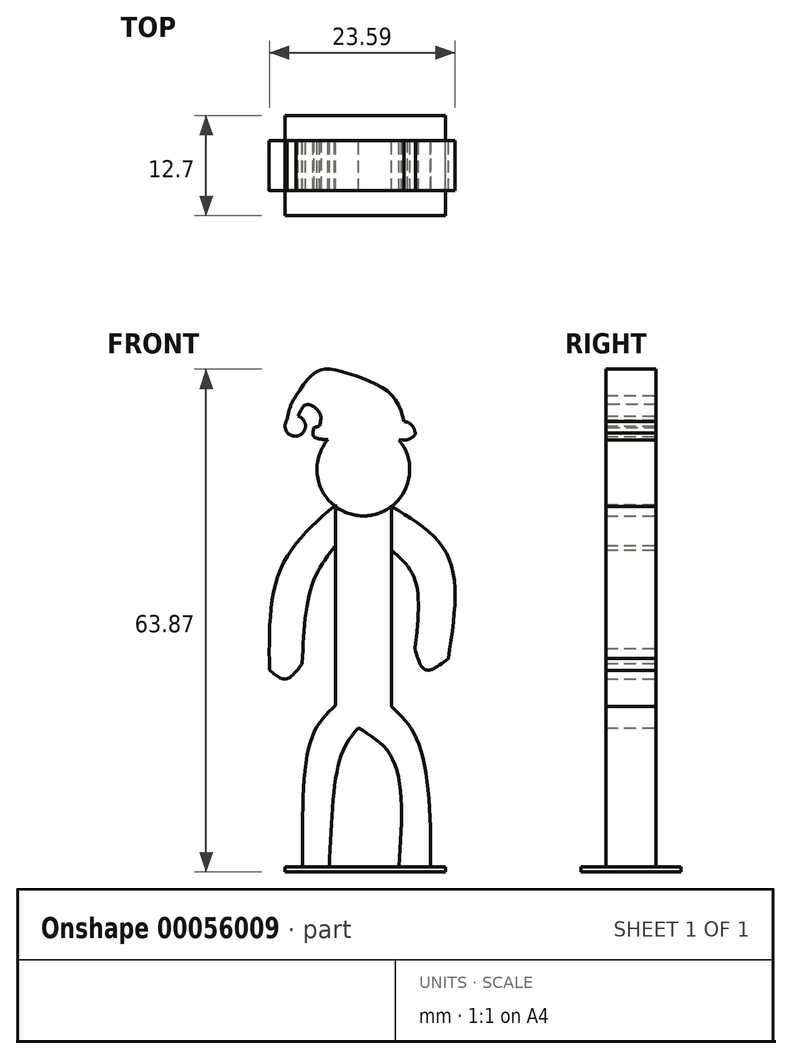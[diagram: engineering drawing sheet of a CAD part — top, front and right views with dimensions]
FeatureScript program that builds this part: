
annotation { "Feature Type Name" : "Feature", "Feature Type Description" : "" }
export const myFeature = defineFeature(function(context is Context, id is Id, definition is map)
    precondition{}
    {
        {
            var Q0;
            Q0=qCreatedBy(makeId("Front.planeOp"),FACE);
            var sketch = newSketch(context, id + "F0", { "sketchPlane" : qUnion([Q0])});
            skFitSpline(sketch, "E0", {"points": [v(8.78, 51.91) * mm, v(1.84, 43.84) * mm, v(0.38, 30.92) * mm], "startDerivative": vector(-17.42, -15.2) * mm, "endDerivative": vector(0.33, -26.61) * mm});
            skFitSpline(sketch, "E1", {"points": [v(15.91, 51.68) * mm, v(23.1, 45.3) * mm, v(23.1, 32.37) * mm], "startDerivative": vector(19.1, -11.4) * mm, "endDerivative": vector(-4.16, -26.82) * mm});
            skFitSpline(sketch, "E2", {"points": [v(15.91, 46.14) * mm, v(18.86, 42.38) * mm, v(18.86, 33.63) * mm], "startDerivative": vector(8.41, -7.48) * mm, "endDerivative": vector(-2, -17.05) * mm});
            skFitSpline(sketch, "E3", {"points": [v(8.78, 46.73) * mm, v(5.8, 41.75) * mm, v(4.55, 31.75) * mm], "startDerivative": vector(-7.92, -10.28) * mm, "endDerivative": vector(-0.86, -19.32) * mm});
            skFitSpline(sketch, "E4", {"points": [v(0.38, 30.92) * mm, v(2.47, 29.78) * mm, v(4.55, 31.75) * mm], "startDerivative": vector(4.49, -3.84) * mm, "endDerivative": vector(3.86, 5.36) * mm});
            skFitSpline(sketch, "E5", {"points": [v(18.86, 33.63) * mm, v(20.26, 30.92) * mm, v(23.1, 32.37) * mm], "startDerivative": vector(2.14, -7.53) * mm, "endDerivative": vector(6.3, 4.98) * mm});
            skLineSegment(sketch, "E6", {"start": v(8.78, 51.91) * mm, "end": v(8.78, 26.4) * mm});
            skLineSegment(sketch, "E7", {"start": v(15.91, 51.68) * mm, "end": v(15.91, 26.28) * mm});
            skCircle(sketch, "E8", {"center": v(12.31, 56.38) * mm, "radius": 5.89 * mm});
            skPoint(sketch, "E8.first.point", {"position": v(12.53, 50.5) * mm});
            skPoint(sketch, "E8.second.point", {"position": v(12.53, 62.27) * mm});
            skPoint(sketch, "E8.third.point", {"position": v(6.7, 58.18) * mm});
            skFitSpline(sketch, "E9", {"points": [v(8.78, 26.4) * mm, v(5.78, 22.38) * mm, v(4.6, 5.88) * mm], "startDerivative": vector(-9.61, -8.78) * mm, "endDerivative": vector(0.3, -30.19) * mm});
            skFitSpline(sketch, "E10", {"points": [v(11.68, 23.56) * mm, v(9.47, 20.03) * mm, v(8, 5.88) * mm], "startDerivative": vector(-7, -8) * mm, "endDerivative": vector(-0.97, -25.61) * mm});
            skFitSpline(sketch, "E11", {"points": [v(11.68, 23.56) * mm, v(16.1, 19.44) * mm, v(16.83, 5.88) * mm], "startDerivative": vector(13, -7.85) * mm, "endDerivative": vector(-1.72, -26.3) * mm});
            skLineSegment(sketch, "E12", {"start": v(4.6, 5.88) * mm, "end": v(8, 5.88) * mm});
            skLineSegment(sketch, "E13", {"start": v(16.83, 5.88) * mm, "end": v(20.85, 5.88) * mm});
            skFitSpline(sketch, "E14", {"points": [v(15.91, 26.28) * mm, v(19.23, 21.79) * mm, v(20.85, 5.88) * mm], "startDerivative": vector(10.22, -9.6) * mm, "endDerivative": vector(-0.4, -29.23) * mm});
            skLineSegment(sketch, "E15", {"start": v(15.91, 51.68) * mm, "end": v(15.91, 51.72) * mm});
            skFitSpline(sketch, "E16", {"points": [v(12.53, 62.27) * mm, v(8.43, 62.27) * mm, v(6, 61.68) * mm], "startDerivative": vector(-7.8, 0.38) * mm, "endDerivative": vector(-5.13, -1.63) * mm});
            skFitSpline(sketch, "E17", {"points": [v(6, 61.68) * mm, v(6, 60.56) * mm, v(7.83, 60.2) * mm, v(11.03, 60.2) * mm, v(17.84, 60.13) * mm], "startDerivative": vector(-2.03, -8.37) * mm, "endDerivative": vector(19.53, -0.22) * mm});
            skFitSpline(sketch, "E18", {"points": [v(17.84, 60.13) * mm, v(18.83, 60.75) * mm, v(18.9, 61.18) * mm], "startDerivative": vector(2.04, 0.95) * mm, "endDerivative": vector(-0.1, 1.17) * mm});
            skFitSpline(sketch, "E19", {"points": [v(12.53, 62.27) * mm, v(18.15, 62.27) * mm, v(18.91, 61.03) * mm], "startDerivative": vector(10.54, 1.21) * mm, "endDerivative": vector(1.2, -4.27) * mm});
            skFitSpline(sketch, "E20", {"points": [v(17.5, 62.48) * mm, v(15.71, 66.04) * mm, v(10.2, 68.63) * mm, v(6.64, 68.94) * mm, v(3.75, 65.78) * mm], "startDerivative": vector(-4.63, 16.24) * mm, "endDerivative": vector(-11.04, -16.4) * mm});
            skFitSpline(sketch, "E21", {"points": [v(6.76, 61.92) * mm, v(6.76, 63.55) * mm, v(5.1, 64.64) * mm, v(4.01, 63.15) * mm], "startDerivative": vector(1.3, 5.19) * mm, "endDerivative": vector(-2.54, -6.29) * mm});
            skFitSpline(sketch, "E22", {"points": [v(3.75, 65.78) * mm, v(3, 64.3) * mm, v(2.61, 62.67) * mm], "startDerivative": vector(-1.67, -2.92) * mm, "endDerivative": vector(-0.61, -3.3) * mm});
            skCircle(sketch, "E23", {"center": v(3.66, 61.9) * mm, "radius": 1.3 * mm});
            skPoint(sketch, "E23.third.point", {"position": v(4.01, 60.66) * mm});
            skLineSegment(sketch, "E24", {"start": v(6.76, 61.92) * mm, "end": v(6.76, 61.91) * mm});
            skLineSegment(sketch, "E25", {"start": v(8.78, 37.79) * mm, "end": v(15.91, 37.79) * mm});
            skLineSegment(sketch, "E26", {"start": v(2.38, 5.88) * mm, "end": v(15.3, 5.88) * mm});
            skPoint(sketch, "E26.endSnap0", {"position": v(6.3, 5.88) * mm});
            skLineSegment(sketch, "E27", {"start": v(15.3, 5.88) * mm, "end": v(22.72, 5.88) * mm});
            skLineSegment(sketch, "E28", {"start": v(2.38, 5.88) * mm, "end": v(2.38, 5.27) * mm});
            skLineSegment(sketch, "E29", {"start": v(2.38, 5.27) * mm, "end": v(22.72, 5.27) * mm});
            skLineSegment(sketch, "E30", {"start": v(22.72, 5.27) * mm, "end": v(22.72, 5.88) * mm});
            skSolve(sketch);
        }
        {
            var Q0;
            {var subQ1=sQuery(id+"F0.wireOp",EDGE,"E20");Q0=makeQuery(id+"F0.imprint","IMPRINT",FACE,{"disambiguationData":[TD([[makeQuery(id+"F0.imprint","IMPRINT",EDGE,{"derivedFrom":subQ1}),1.0]])]});}
            var Q1;
            {var subQ0=sQuery(id+"F0.wireOp",EDGE,"E16");var subQ3=sQuery(id+"F0.wireOp",EDGE,"E17");var subQ5=makeQuery(id+"F0.imprint","INTERSECT",VERTEX,{"derivedFrom":[subQ0,subQ3]});Q1=makeQuery(id+"F0.imprint","IMPRINT",FACE,{"disambiguationData":[TD([[makeQuery(id+"F0.imprint","IMPRINT",EDGE,{"disambiguationData":[TD([[subQ5,1.0]])],"derivedFrom":subQ0}),1.0]])]});}
            var Q2;
            {var subQ0=sQuery(id+"F0.wireOp",EDGE,"E23");var subQ1=makeQuery(id+"F0.imprint","INTERSECT",VERTEX,{"derivedFrom":[sQuery(id+"F0.wireOp",EDGE,"E21"),subQ0]});Q2=makeQuery(id+"F0.imprint","IMPRINT",FACE,{"disambiguationData":[TD([[makeQuery(id+"F0.imprint","IMPRINT",EDGE,{"disambiguationData":[TD([[subQ1,-1.0]])],"derivedFrom":subQ0}),1.0]])]});}
            var Q3;
            {var subQ0=sQuery(id+"F0.wireOp",EDGE,"E8");var subQ2=sQuery(id+"F0.wireOp",EDGE,"E17");var subQ3=makeQuery(id+"F0.imprint","INTERSECT",VERTEX,{"disambiguationData":[OD(0.0)],"derivedFrom":[subQ0,subQ2]});Q3=makeQuery(id+"F0.imprint","IMPRINT",FACE,{"disambiguationData":[TD([[makeQuery(id+"F0.imprint","IMPRINT",EDGE,{"disambiguationData":[TD([[subQ3,1.0]])],"derivedFrom":subQ2}),1.0]])]});}
            var Q4;
            {var subQ4=sQuery(id+"F0.wireOp",EDGE,"E18");var subQ5=sQuery(id+"F0.wireOp",EDGE,"E17");var subQ6=makeQuery(id+"F0.imprint","INTERSECT",VERTEX,{"derivedFrom":[subQ5,subQ4]});Q4=makeQuery(id+"F0.imprint","IMPRINT",FACE,{"disambiguationData":[TD([[makeQuery(id+"F0.imprint","IMPRINT",EDGE,{"disambiguationData":[TD([[subQ6,1.0]])],"derivedFrom":subQ5}),1.0]])]});}
            extrude(context, id + "F1", {"entities" : qUnion([Q0, Q1, Q2, Q3, Q4]), "depth" : 6.35 * mm});
        }
        {
            var Q0;
            {var subQ1=sQuery(id+"F0.wireOp",EDGE,"E0");var subQ5=sQuery(id+"F0.wireOp",EDGE,"E6");var subQ6=makeQuery(id+"F0.imprint","INTERSECT",VERTEX,{"derivedFrom":[subQ1,subQ5]});Q0=makeQuery(id+"F0.imprint","IMPRINT",FACE,{"disambiguationData":[TD([[makeQuery(id+"F0.imprint","IMPRINT",EDGE,{"disambiguationData":[TD([[subQ6,-1.0]])],"derivedFrom":subQ1}),-1.0]])]});}
            var Q1;
            {var subQ1=sQuery(id+"F0.wireOp",EDGE,"E3");Q1=makeQuery(id+"F0.imprint","IMPRINT",FACE,{"disambiguationData":[TD([[makeQuery(id+"F0.imprint","IMPRINT",EDGE,{"derivedFrom":subQ1}),-1.0]])]});}
            var Q2;
            {var subQ0=sQuery(id+"F0.wireOp",EDGE,"E1");Q2=makeQuery(id+"F0.imprint","IMPRINT",FACE,{"disambiguationData":[TD([[makeQuery(id+"F0.imprint","IMPRINT",EDGE,{"derivedFrom":subQ0}),-1.0]])]});}
            extrude(context, id + "F2", {"entities" : qUnion([Q0, Q1, Q2]), "operationType" : NewBodyOperationType.ADD, "depth" : 6.35 * mm});
        }
        {
            var Q0;
            {var subQ3=sQuery(id+"F0.wireOp",EDGE,"E15");Q0=makeQuery(id+"F0.imprint","IMPRINT",FACE,{"disambiguationData":[TD([[makeQuery(id+"F0.imprint","IMPRINT",EDGE,{"derivedFrom":subQ3}),1.0]])]});}
            var Q1;
            {var subQ1=sQuery(id+"F0.wireOp",EDGE,"E9");Q1=makeQuery(id+"F0.imprint","IMPRINT",FACE,{"disambiguationData":[TD([[makeQuery(id+"F0.imprint","IMPRINT",EDGE,{"derivedFrom":subQ1}),1.0]])]});}
            extrude(context, id + "F3", {"entities" : qUnion([Q0, Q1]), "depth" : 6.35 * mm});
        }
        {
            var Q0;
            {var subQ6=sQuery(id+"F0.wireOp",EDGE,"E28");Q0=makeQuery(id+"F0.imprint","IMPRINT",FACE,{"disambiguationData":[TD([[makeQuery(id+"F0.imprint","IMPRINT",EDGE,{"derivedFrom":subQ6}),1.0]])]});}
            extrude(context, id + "F4", {"entities" : qUnion([Q0]), "operationType" : NewBodyOperationType.ADD, "depth" : 9.52 * mm, "hasSecondDirection" : true, "secondDirectionOppositeDirection" : true, "secondDirectionDepth" : 3.17 * mm});
        }
    });
